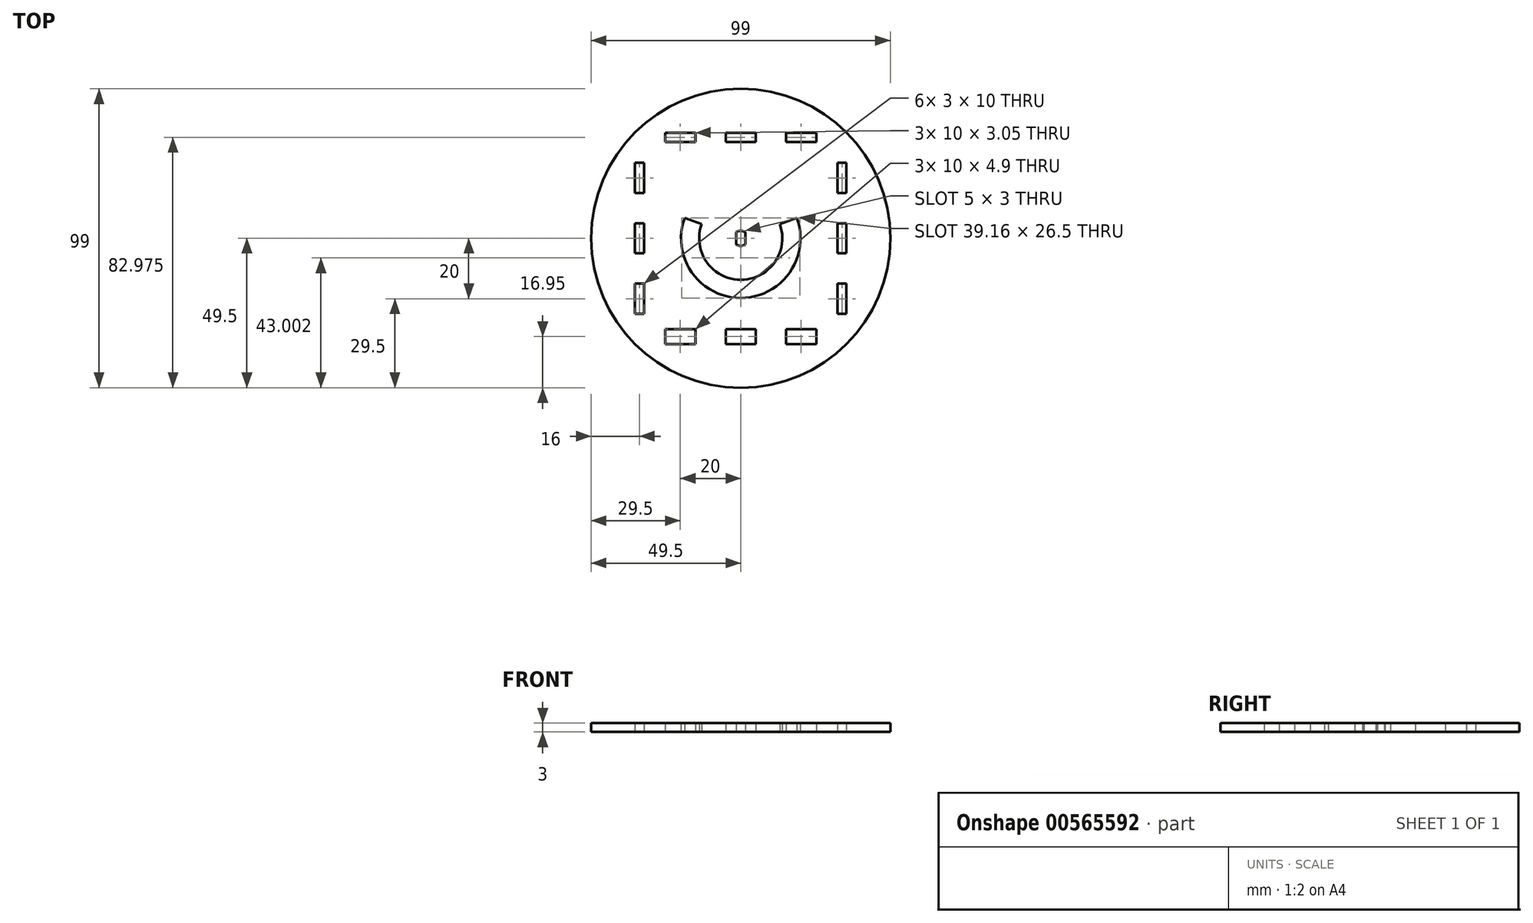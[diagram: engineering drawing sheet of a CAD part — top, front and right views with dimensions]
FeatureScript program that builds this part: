
annotation { "Feature Type Name" : "Feature", "Feature Type Description" : "" }
export const myFeature = defineFeature(function(context is Context, id is Id, definition is map)
    precondition{}
    {
        {
            var Q0;
            Q0=qCreatedBy(makeId("Top.planeOp"),FACE);
            var sketch = newSketch(context, id + "F0", { "sketchPlane" : qUnion([Q0])});
            skCircle(sketch, "E0.cCircle", {"center": v(0, 0) * mm, "radius": 49.5 * mm});
            skLineSegment(sketch, "E1.top", {"start": v(-25, 31.95) * mm, "end": v(-15, 31.95) * mm});
            skLineSegment(sketch, "E1.left", {"start": v(-25, 35) * mm, "end": v(-25, 31.95) * mm});
            skLineSegment(sketch, "E1.right", {"start": v(-15, 35) * mm, "end": v(-15, 31.95) * mm});
            skLineSegment(sketch, "E2.bottom", {"start": v(-5, 35) * mm, "end": v(5, 35) * mm});
            skLineSegment(sketch, "E2.top", {"start": v(-5, 31.95) * mm, "end": v(5, 31.95) * mm});
            skLineSegment(sketch, "E2.left", {"start": v(-5, 35) * mm, "end": v(-5, 31.95) * mm});
            skLineSegment(sketch, "E2.right", {"start": v(5, 35) * mm, "end": v(5, 31.95) * mm});
            skLineSegment(sketch, "E3.top", {"start": v(15, 31.95) * mm, "end": v(25, 31.95) * mm});
            skLineSegment(sketch, "E3.left", {"start": v(15, 35) * mm, "end": v(15, 31.95) * mm});
            skLineSegment(sketch, "E3.right", {"start": v(25, 35) * mm, "end": v(25, 31.95) * mm});
            skLineSegment(sketch, "E4.bottom", {"start": v(-35, 25) * mm, "end": v(-32, 25) * mm});
            skLineSegment(sketch, "E4.top", {"start": v(-35, 15) * mm, "end": v(-32, 15) * mm});
            skLineSegment(sketch, "E4.left", {"start": v(-35, 25) * mm, "end": v(-35, 15) * mm});
            skLineSegment(sketch, "E4.right", {"start": v(-32, 25) * mm, "end": v(-32, 15) * mm});
            skLineSegment(sketch, "E5.bottom", {"start": v(-35, 5) * mm, "end": v(-32, 5) * mm});
            skLineSegment(sketch, "E5.top", {"start": v(-35, -5) * mm, "end": v(-32, -5) * mm});
            skLineSegment(sketch, "E5.left", {"start": v(-35, 5) * mm, "end": v(-35, -5) * mm});
            skLineSegment(sketch, "E5.right", {"start": v(-32, 5) * mm, "end": v(-32, -5) * mm});
            skLineSegment(sketch, "E6.bottom", {"start": v(-35, -15) * mm, "end": v(-32, -15) * mm});
            skLineSegment(sketch, "E6.top", {"start": v(-35, -25) * mm, "end": v(-32, -25) * mm});
            skLineSegment(sketch, "E6.left", {"start": v(-35, -15) * mm, "end": v(-35, -25) * mm});
            skLineSegment(sketch, "E6.right", {"start": v(-32, -15) * mm, "end": v(-32, -25) * mm});
            skLineSegment(sketch, "E7.bottom", {"start": v(35, 25) * mm, "end": v(32, 25) * mm});
            skLineSegment(sketch, "E7.top", {"start": v(35, 15) * mm, "end": v(32, 15) * mm});
            skLineSegment(sketch, "E7.left", {"start": v(35, 25) * mm, "end": v(35, 15) * mm});
            skLineSegment(sketch, "E7.right", {"start": v(32, 25) * mm, "end": v(32, 15) * mm});
            skLineSegment(sketch, "E8.bottom", {"start": v(35, 5) * mm, "end": v(32, 5) * mm});
            skLineSegment(sketch, "E8.top", {"start": v(35, -5) * mm, "end": v(32, -5) * mm});
            skLineSegment(sketch, "E8.left", {"start": v(35, 5) * mm, "end": v(35, -5) * mm});
            skLineSegment(sketch, "E8.right", {"start": v(32, 5) * mm, "end": v(32, -5) * mm});
            skLineSegment(sketch, "E9.bottom", {"start": v(32, -15) * mm, "end": v(35, -15) * mm});
            skLineSegment(sketch, "E9.top", {"start": v(32, -25) * mm, "end": v(35, -25) * mm});
            skLineSegment(sketch, "E9.left", {"start": v(32, -15) * mm, "end": v(32, -25) * mm});
            skLineSegment(sketch, "E9.right", {"start": v(35, -15) * mm, "end": v(35, -25) * mm});
            skLineSegment(sketch, "E10", {"start": v(25, 35) * mm, "end": v(15, 35) * mm});
            skLineSegment(sketch, "E11", {"start": v(-15, 35) * mm, "end": v(-25, 35) * mm});
            skLineSegment(sketch, "E12.bottom", {"start": v(-25, -35) * mm, "end": v(-15, -35) * mm});
            skLineSegment(sketch, "E12.top", {"start": v(-25, -30.1) * mm, "end": v(-15, -30.1) * mm});
            skLineSegment(sketch, "E12.left", {"start": v(-25, -35) * mm, "end": v(-25, -30.1) * mm});
            skLineSegment(sketch, "E12.right", {"start": v(-15, -35) * mm, "end": v(-15, -30.1) * mm});
            skLineSegment(sketch, "E13.bottom", {"start": v(-5, -35) * mm, "end": v(5, -35) * mm});
            skLineSegment(sketch, "E13.top", {"start": v(-5, -30.1) * mm, "end": v(5, -30.1) * mm});
            skLineSegment(sketch, "E13.left", {"start": v(-5, -35) * mm, "end": v(-5, -30.1) * mm});
            skLineSegment(sketch, "E13.right", {"start": v(5, -35) * mm, "end": v(5, -30.1) * mm});
            skLineSegment(sketch, "E14.bottom", {"start": v(15, -35) * mm, "end": v(25, -35) * mm});
            skLineSegment(sketch, "E14.top", {"start": v(15, -30.1) * mm, "end": v(25, -30.1) * mm});
            skLineSegment(sketch, "E14.left", {"start": v(15, -35) * mm, "end": v(15, -30.1) * mm});
            skLineSegment(sketch, "E14.right", {"start": v(25, -35) * mm, "end": v(25, -30.1) * mm});
            skArc(sketch, "E15", {"start": v(1.5, 2) * mm, "mid": v(0, 2.5) * mm, "end": v(-1.5, 2) * mm});
            skLineSegment(sketch, "E16.left", {"start": v(1.5, -2) * mm, "end": v(1.5, 2) * mm});
            skLineSegment(sketch, "E16.right", {"start": v(-1.5, -2) * mm, "end": v(-1.5, 2) * mm});
            skPoint(sketch, "E17.orphan", {"position": v(-1.5, -2.33) * mm});
            skPoint(sketch, "E18.orphan", {"position": v(1.5, -2.36) * mm});
            skPoint(sketch, "E19.orphan", {"position": v(1.5, 2.33) * mm});
            skPoint(sketch, "E20.orphan", {"position": v(-1.5, 2.36) * mm});
            skArc(sketch, "E21", {"start": v(-18.56, 6.75) * mm, "mid": v(0, -19.75) * mm, "end": v(18.56, 6.75) * mm});
            skArc(sketch, "E22", {"start": v(-12.92, 4.7) * mm, "mid": v(0, -13.75) * mm, "end": v(12.92, 4.7) * mm});
            skLineSegment(sketch, "E23", {"start": v(-18.56, 6.75) * mm, "end": v(-12.92, 4.7) * mm});
            skLineSegment(sketch, "E24", {"start": v(18.56, 6.75) * mm, "end": v(12.92, 4.7) * mm});
            skArc(sketch, "E25.trimOffspring", {"start": v(-1.5, -2) * mm, "mid": v(0, -2.5) * mm, "end": v(1.5, -2) * mm});
            skSolve(sketch);
        }
        {
            var Q0;
            Q0 = qSketchRegion(id + "F0", true);
            var Q1;
            {var subQ0=sQuery(id+"F0.wireOp",EDGE,"E16.right");Q1=makeQuery(id+"F0.imprint","IMPRINT",FACE,{"disambiguationData":[TD([[makeQuery(id+"F0.imprint","IMPRINT",EDGE,{"derivedFrom":subQ0}),1.0]])]});}
            var Q2;
            {var subQ0=sQuery(id+"F0.wireOp",EDGE,"E16.left");Q2=makeQuery(id+"F0.imprint","IMPRINT",FACE,{"disambiguationData":[TD([[makeQuery(id+"F0.imprint","IMPRINT",EDGE,{"derivedFrom":subQ0}),-1.0]])]});}
            var Q3;
            {var subQ5=sQuery(id+"F0.wireOp",EDGE,"E15");var subQ6=makeQuery(id+"F0.imprint","INTERSECT",VERTEX,{"disambiguationData":[OD(1.0)],"derivedFrom":[subQ5,sQuery(id+"F0.wireOp",EDGE,"E16.left")]});Q3=makeQuery(id+"F0.imprint","IMPRINT",FACE,{"disambiguationData":[TD([[makeQuery(id+"F0.imprint","IMPRINT",EDGE,{"disambiguationData":[TD([[subQ6,1.0]])],"derivedFrom":subQ5}),-1.0]])]});}
            var Q4;
            {var subQ0=sQuery(id+"F0.wireOp",EDGE,"E15");var subQ4=makeQuery(id+"F0.imprint","INTERSECT",VERTEX,{"disambiguationData":[OD(0.0)],"derivedFrom":[subQ0,sQuery(id+"F0.wireOp",EDGE,"E16.right")]});Q4=makeQuery(id+"F0.imprint","IMPRINT",FACE,{"disambiguationData":[TD([[makeQuery(id+"F0.imprint","IMPRINT",EDGE,{"disambiguationData":[TD([[subQ4,1.0]])],"derivedFrom":subQ0}),-1.0]])]});}
            extrude(context, id + "F1", {"entities" : qUnion([Q0, Q1, Q2, Q3, Q4]), "depth" : 3 * mm, "offsetDistance" : 25 * mm});
        }
    });
